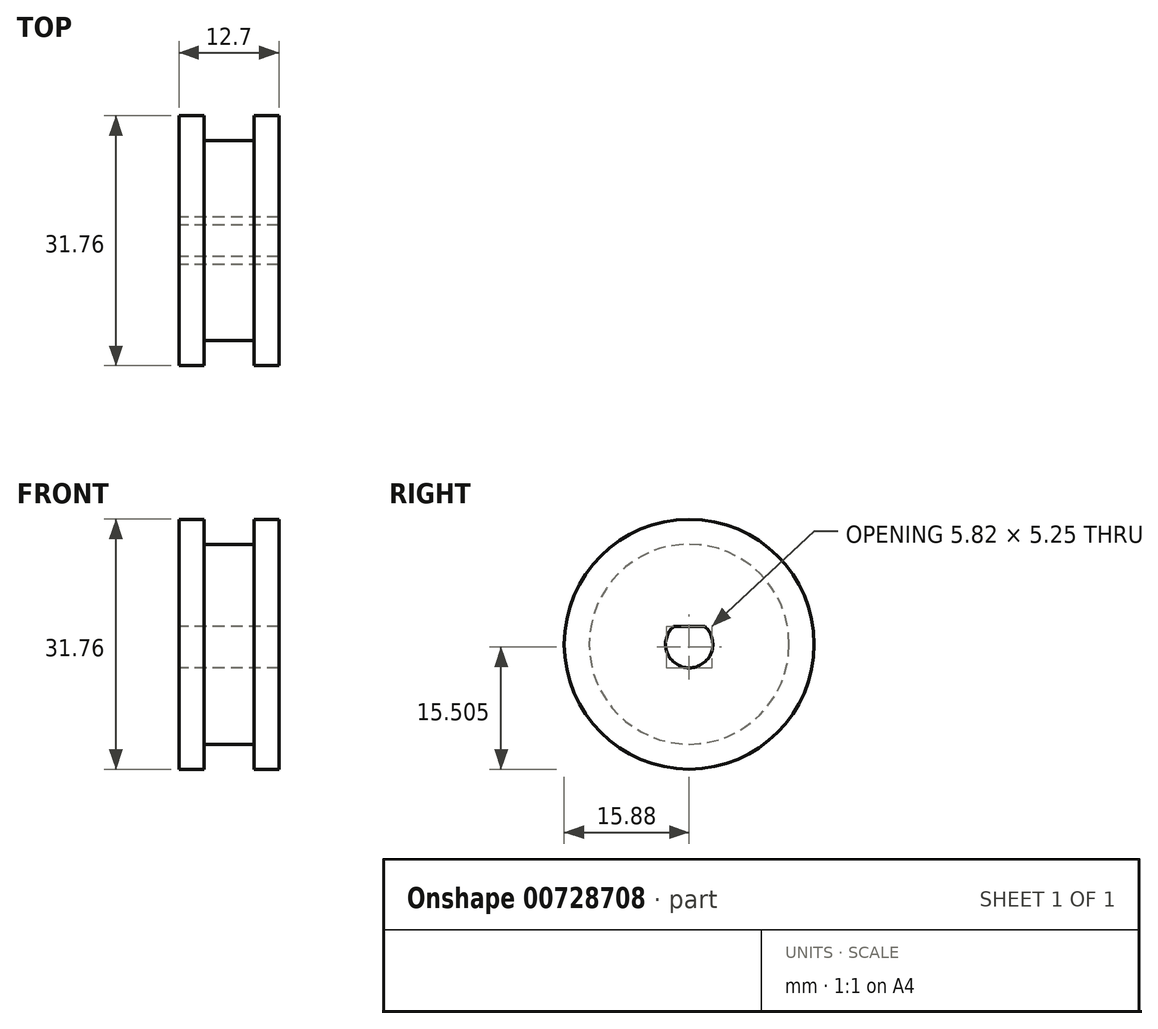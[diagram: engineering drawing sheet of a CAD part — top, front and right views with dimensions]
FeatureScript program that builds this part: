
annotation { "Feature Type Name" : "Feature", "Feature Type Description" : "" }
export const myFeature = defineFeature(function(context is Context, id is Id, definition is map)
    precondition{}
    {
        {
            var Q0;
            Q0=qCreatedBy(makeId("Front.planeOp"),FACE);
            var sketch = newSketch(context, id + "F0", { "sketchPlane" : qUnion([Q0])});
            skLineSegment(sketch, "E0", {"start": v(-15.1, 0) * mm, "end": v(15.1, 0) * mm, "construction": true});
            skLineSegment(sketch, "E1", {"start": v(-6.35, 3) * mm, "end": v(-6.35, 15.88) * mm});
            skLineSegment(sketch, "E2", {"start": v(-6.35, 15.88) * mm, "end": v(-3.17, 15.88) * mm});
            skLineSegment(sketch, "E3", {"start": v(-3.17, 15.88) * mm, "end": v(-3.17, 12.7) * mm});
            skLineSegment(sketch, "E4", {"start": v(-3.17, 12.7) * mm, "end": v(3.17, 12.7) * mm});
            skLineSegment(sketch, "E5", {"start": v(3.17, 12.7) * mm, "end": v(3.17, 15.88) * mm});
            skLineSegment(sketch, "E6", {"start": v(3.17, 15.88) * mm, "end": v(6.35, 15.88) * mm});
            skLineSegment(sketch, "E7", {"start": v(6.35, 15.88) * mm, "end": v(6.35, 3) * mm});
            skLineSegment(sketch, "E8", {"start": v(6.35, 3) * mm, "end": v(-6.35, 3) * mm});
            skPoint(sketch, "E9", {"position": v(0, 12.7) * mm});
            skSolve(sketch);
        }
        {
            var Q0;
            Q0=qSketchRegion(id+"F0",true);
            var Q1;
            Q1=sQuery(id+"F0.wireOp",EDGE,"E0");
            revolve(context, id + "F1", {"surfaceOperationType" : NewSurfaceOperationType.NEW, "entities" : qUnion([Q0]), "axis" : qUnion([Q1]), "revolveType" : RevolveType.FULL});
        }
        {
            var Q0;
            Q0=qCreatedBy(makeId("Right.planeOp"),FACE);
            var sketch = newSketch(context, id + "F2", { "sketchPlane" : qUnion([Q0])});
            skArc(sketch, "E10.0", {"start": v(1.98, 2.25) * mm, "mid": v(0, 3) * mm, "end": v(-1.98, 2.25) * mm});
            skLineSegment(sketch, "E11", {"start": v(-1.98, 2.25) * mm, "end": v(1.98, 2.25) * mm});
            skSolve(sketch);
        }
        {
            var Q0;
            Q0=qSketchRegion(id+"F2",true);
            var Q1;
            Q1=makeQuery(id+"F1.opRevolve","SWEPT_FACE",FACE,{"disambiguationData":[OSD([sQuery(id+"F0.wireOp",EDGE,"E7")])]});
            var Q2;
            Q2=makeQuery(id+"F1.opRevolve","SWEPT_FACE",FACE,{"disambiguationData":[OSD([sQuery(id+"F0.wireOp",EDGE,"E1")])]});
            extrude(context, id + "F3", {"entities" : qUnion([Q0]), "operationType" : NewBodyOperationType.ADD, "endBound" : BoundingType.UP_TO_SURFACE, "depth" : 25.4 * mm, "endBoundEntityFace" : qUnion([Q1]), "offsetDistance" : 25.4 * mm, "hasSecondDirection" : true, "secondDirectionBound" : BoundingType.UP_TO_SURFACE, "secondDirectionOppositeDirection" : true, "secondDirectionDepth" : 25.4 * mm, "secondDirectionBoundEntityFace" : qUnion([Q2])});
        }
    });
